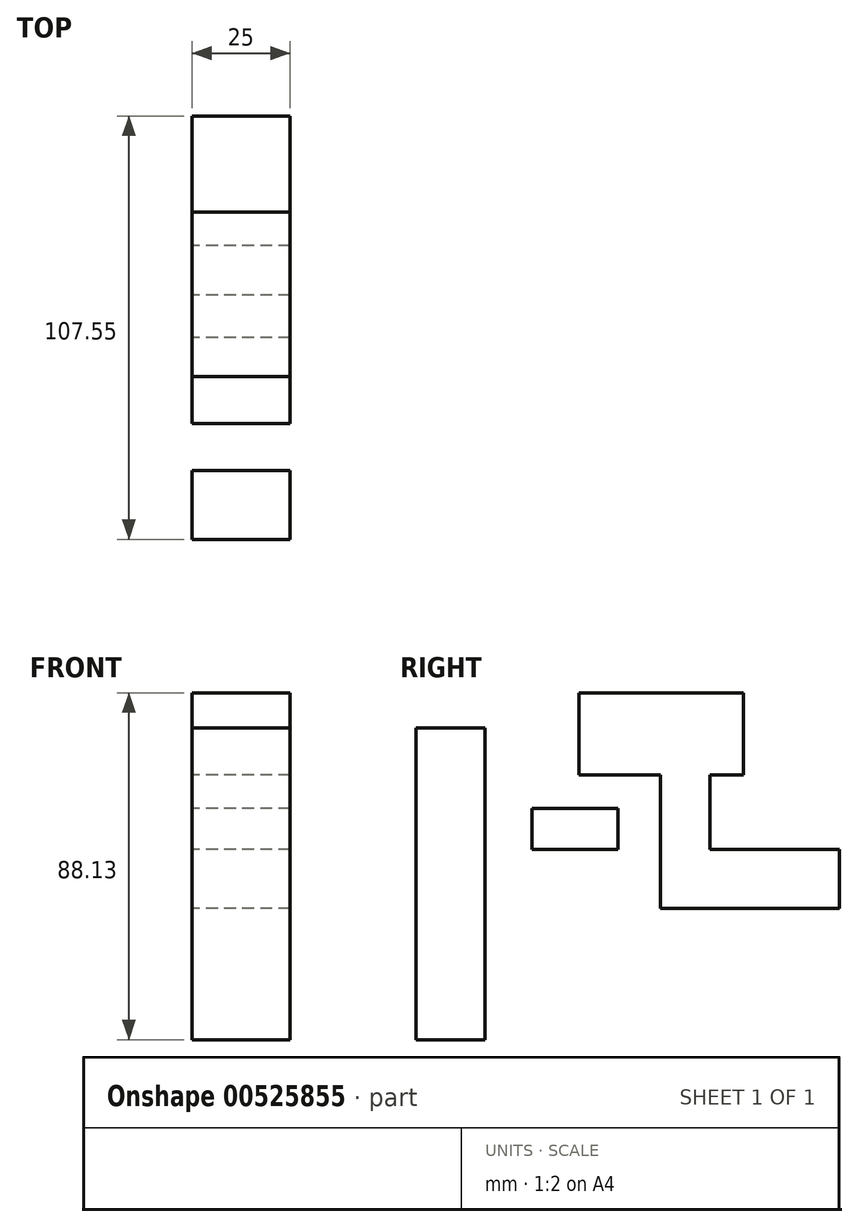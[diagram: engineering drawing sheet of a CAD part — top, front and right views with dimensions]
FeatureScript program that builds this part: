
annotation { "Feature Type Name" : "Feature", "Feature Type Description" : "" }
export const myFeature = defineFeature(function(context is Context, id is Id, definition is map)
    precondition{}
    {
        {
            var Q0;
            Q0=qCreatedBy(makeId("Right.planeOp"),FACE);
            var sketch = newSketch(context, id + "F0", { "sketchPlane" : qUnion([Q0])});
            skLineSegment(sketch, "E0.bottom", {"start": v(-62.02, 51.42) * mm, "end": v(-44.6, 51.42) * mm});
            skLineSegment(sketch, "E0.top", {"start": v(-62.02, -27.75) * mm, "end": v(-44.6, -27.75) * mm});
            skLineSegment(sketch, "E0.left", {"start": v(-62.02, 51.42) * mm, "end": v(-62.02, -27.75) * mm});
            skLineSegment(sketch, "E0.right", {"start": v(-44.6, 51.42) * mm, "end": v(-44.6, -27.75) * mm});
            skLineSegment(sketch, "E1.bottom", {"start": v(-32.64, 31) * mm, "end": v(-10.74, 31) * mm});
            skLineSegment(sketch, "E1.top", {"start": v(-32.64, 20.55) * mm, "end": v(-10.74, 20.55) * mm});
            skLineSegment(sketch, "E1.left", {"start": v(-32.64, 31) * mm, "end": v(-32.64, 20.55) * mm});
            skLineSegment(sketch, "E1.right", {"start": v(-10.74, 31) * mm, "end": v(-10.74, 20.55) * mm});
            skLineSegment(sketch, "E2.bottom", {"start": v(-20.7, 39.47) * mm, "end": v(21.13, 39.47) * mm});
            skLineSegment(sketch, "E2.top", {"start": v(-20.7, 60.38) * mm, "end": v(21.13, 60.38) * mm});
            skLineSegment(sketch, "E2.left", {"start": v(-20.7, 39.47) * mm, "end": v(-20.7, 60.38) * mm});
            skLineSegment(sketch, "E2.right", {"start": v(21.13, 39.47) * mm, "end": v(21.13, 60.38) * mm});
            skLineSegment(sketch, "E3.bottom", {"start": v(0, 39.47) * mm, "end": v(12.66, 39.47) * mm});
            skLineSegment(sketch, "E3.top", {"start": v(0, 5.61) * mm, "end": v(12.66, 5.61) * mm});
            skLineSegment(sketch, "E3.left", {"start": v(0, 39.47) * mm, "end": v(0, 5.61) * mm});
            skLineSegment(sketch, "E3.right", {"start": v(12.66, 39.47) * mm, "end": v(12.66, 5.61) * mm});
            skLineSegment(sketch, "E4.bottom", {"start": v(12.66, 20.55) * mm, "end": v(45.53, 20.55) * mm});
            skLineSegment(sketch, "E4.top", {"start": v(12.66, 5.61) * mm, "end": v(45.53, 5.61) * mm});
            skLineSegment(sketch, "E4.left", {"start": v(12.66, 20.55) * mm, "end": v(12.66, 5.61) * mm});
            skLineSegment(sketch, "E4.right", {"start": v(45.53, 20.55) * mm, "end": v(45.53, 5.61) * mm});
            skSolve(sketch);
        }
        {
            var Q0;
            Q0 = qSketchRegion(id + "F0", true);
            extrude(context, id + "F1", {"entities" : qUnion([Q0]), "depth" : 25 * mm, "offsetDistance" : 25 * mm});
        }
    });
